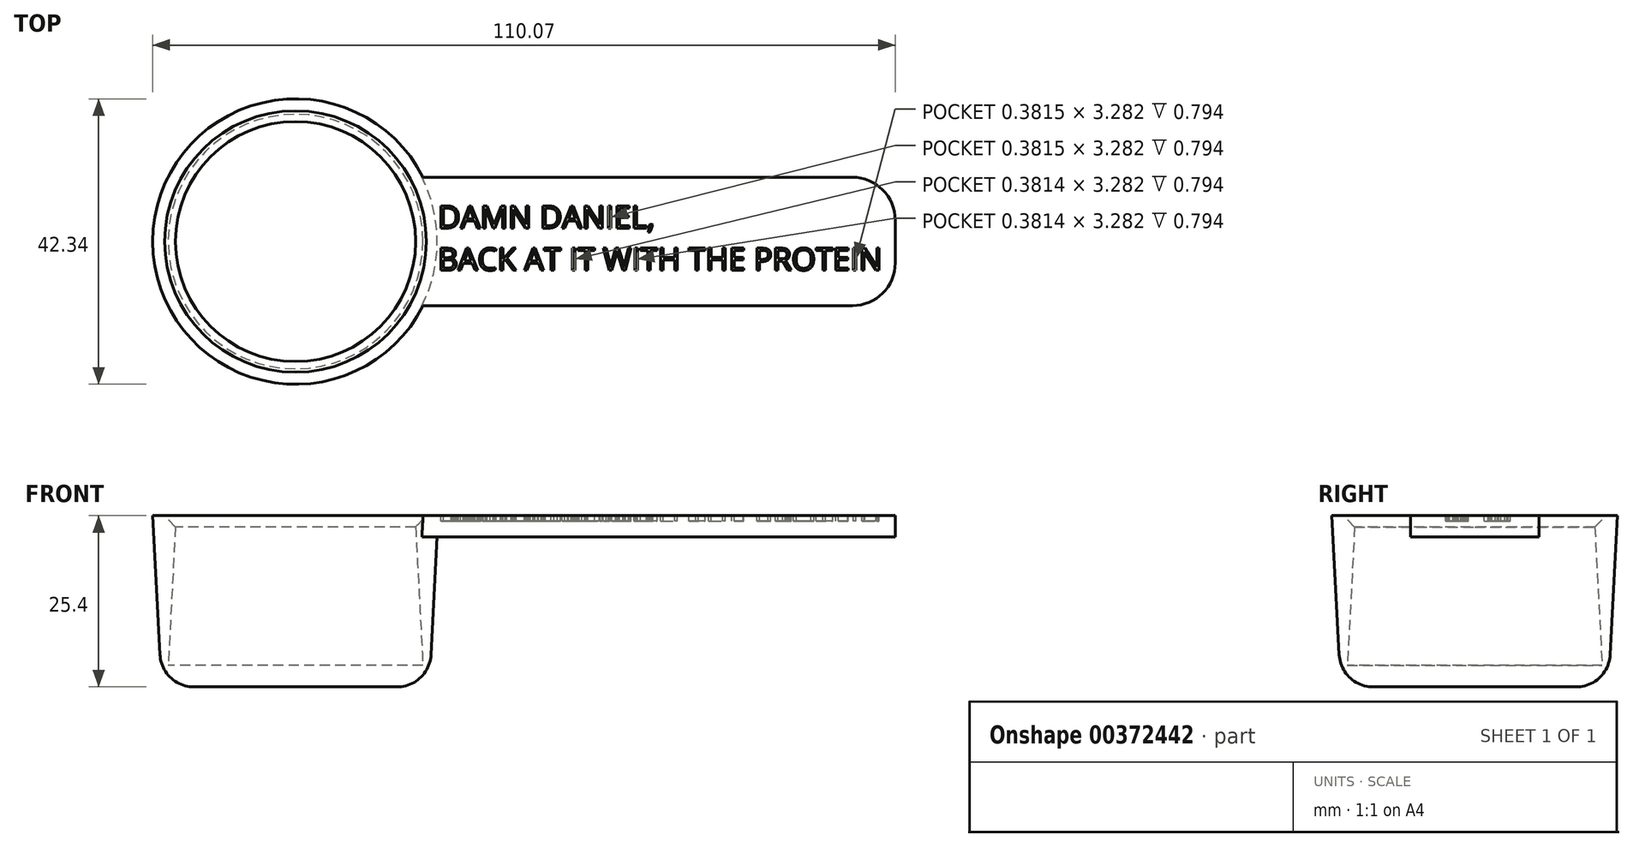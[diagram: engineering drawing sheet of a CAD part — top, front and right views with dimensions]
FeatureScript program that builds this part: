
annotation { "Feature Type Name" : "Feature", "Feature Type Description" : "" }
export const myFeature = defineFeature(function(context is Context, id is Id, definition is map)
    precondition{}
    {
        {
            var Q0;
            Q0=qCreatedBy(makeId("Top.planeOp"),FACE);
            var sketch = newSketch(context, id + "F0", { "sketchPlane" : qUnion([Q0])});
            skCircle(sketch, "E0", {"center": v(0, 0) * mm, "radius": 19.05 * mm});
            skCircle(sketch, "E1", {"center": v(0, 0) * mm, "radius": 19.84 * mm});
            skSolve(sketch);
        }
        {
            var Q0;
            Q0=qSketchRegion(id+"F0",true);
            extrude(context, id + "F1", {"entities" : qUnion([Q0]), "depth" : 25.4 * mm, "hasDraft" : true, "draftAngle" : 3 * degree});
        }
        {
            var Q0;
            Q0=qCreatedBy(makeId("Top.planeOp"),FACE);
            var sketch = newSketch(context, id + "F2", { "sketchPlane" : qUnion([Q0])});
            skCircle(sketch, "E2", {"center": v(0, 0) * mm, "radius": 19.84 * mm});
            skSolve(sketch);
        }
        {
            var Q0;
            Q0=qSketchRegion(id+"F2",true);
            extrude(context, id + "F3", {"entities" : qUnion([Q0]), "operationType" : NewBodyOperationType.ADD, "depth" : 3.17 * mm});
        }
        {
            var Q0;
            Q0=qCreatedBy(makeId("Right.planeOp"),FACE);
            cPlane(context, id + "F4", {"entities" : qUnion([Q0]), "cplaneType" : CPlaneType.OFFSET, "offset" : 88.9 * mm, "width" : 152.4 * mm, "height" : 152.4 * mm});
        }
        {
            var Q0;
            Q0=qCreatedBy(id+"F4.planeOp",FACE);
            var sketch = newSketch(context, id + "F5", { "sketchPlane" : qUnion([Q0])});
            skLineSegment(sketch, "E3", {"start": v(0, 0) * mm, "end": v(0, 25.4) * mm, "construction": true});
            skLineSegment(sketch, "E4", {"start": v(0, 25.4) * mm, "end": v(-9.53, 25.4) * mm});
            skLineSegment(sketch, "E5", {"start": v(-9.53, 25.4) * mm, "end": v(-9.53, 22.23) * mm});
            skLineSegment(sketch, "E6", {"start": v(-9.53, 22.23) * mm, "end": v(9.52, 22.23) * mm});
            skLineSegment(sketch, "E7", {"start": v(9.52, 22.23) * mm, "end": v(9.52, 25.4) * mm});
            skLineSegment(sketch, "E8", {"start": v(9.52, 25.4) * mm, "end": v(0, 25.4) * mm});
            skSolve(sketch);
        }
        {
            var Q0;
            Q0=qSketchRegion(id+"F5",true);
            var Q1;
            Q1=makeQuery(id+"F1.opExtrude","SWEPT_FACE",FACE,{"disambiguationData":[OSD([sQuery(id+"F0.wireOp",EDGE,"E1")])]});
            extrude(context, id + "F6", {"entities" : qUnion([Q0]), "operationType" : NewBodyOperationType.ADD, "endBound" : BoundingType.UP_TO_SURFACE, "oppositeDirection" : true, "endBoundEntityFace" : qUnion([Q1]), "depth" : 25.4 * mm});
        }
        {
            var Q0;
            Q0=makeQuery(id+"F6.opExtrude","CAP_EDGE",EDGE,{"disambiguationData":[OSD([sQuery(id+"F5.wireOp",EDGE,"E5")])],"isStart":true});
            var Q1;
            Q1=makeQuery(id+"F6.opExtrude","CAP_EDGE",EDGE,{"disambiguationData":[OSD([sQuery(id+"F5.wireOp",EDGE,"E7")])],"isStart":true});
            fillet(context, id + "F7", {"entities" : qUnion([Q0, Q1]), "radius" : 6.35 * mm, "tangentPropagation" : true, "allowEdgeOverflow" : false});
        }
        {
            var Q0;
            Q0=makeQuery(id+"F6.boolean.opBoolean","MERGE",FACE,{"derivedFrom":[makeQuery(id+"F1.opExtrude","CAP_FACE",FACE,{"disambiguationData":[OSD([sQuery(id+"F0.wireOp",EDGE,"E0"),sQuery(id+"F0.wireOp",EDGE,"E1")])],"isStart":false}),makeQuery(id+"F6.opExtrude","SWEPT_FACE",FACE,{"disambiguationData":[OSD([sQuery(id+"F5.wireOp",EDGE,"E4"),sQuery(id+"F5.wireOp",EDGE,"E8")])]})]});
            var sketch = newSketch(context, id + "F8", { "sketchPlane" : qUnion([Q0])});
            skText(sketch, "E9", { "text": "DAMN DANIEL, \nBACK AT IT WITH THE PROTEIN", "fontName": "OpenSans-Regular.ttf"});
            const initialGuessF8  = {"E9": [0.02111, 0.00199, 1, 0, 0.00331]};
            skSetInitialGuess(sketch, initialGuessF8);
            skSolve(sketch);
        }
        {
            var Q0;
            Q0=qSketchRegion(id+"F8",true);
            extrude(context, id + "F9", {"entities" : qUnion([Q0]), "operationType" : NewBodyOperationType.REMOVE, "oppositeDirection" : true, "depth" : 0.8 * mm});
        }
        {
            var Q0;
            Q0=makeQuery(id+"F1.opExtrude","CAP_EDGE",EDGE,{"disambiguationData":[OSD([sQuery(id+"F0.wireOp",EDGE,"E0")])],"isStart":false});
            chamfer(context, id + "F10", {"entities" : qUnion([Q0]), "width" : 1.59 * mm, "tangentPropagation" : true});
        }
        {
            var Q0;
            Q0=makeQuery(id+"F1.opExtrude","CAP_EDGE",EDGE,{"disambiguationData":[OSD([sQuery(id+"F0.wireOp",EDGE,"E1")])],"isStart":true});
            fillet(context, id + "F11", {"entities" : qUnion([Q0]), "radius" : 5.08 * mm, "tangentPropagation" : true, "allowEdgeOverflow" : false});
        }
    });
